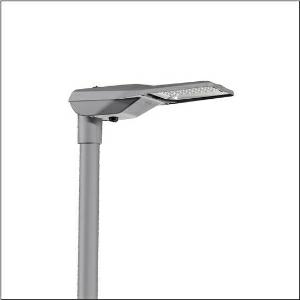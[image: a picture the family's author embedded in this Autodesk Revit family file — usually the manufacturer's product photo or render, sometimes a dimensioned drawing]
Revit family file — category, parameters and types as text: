
# Revit family: streetlight_sl_21_iq_mini___p0_8a_5xe2u31y08gb_4fe4
name_source: partatom
category: Lighting Fixtures
units: mm (PartAtom-declared; Revit-internal decimal feet)

## family parameters
Cut with Voids When Loaded = No
Host = Face
Light Source = No
Part Type = Normal
Room Calculation Point = No
Round Connector Dimension = Use Diameter
Shared = No

## types (1)
- --- (1 x LED, 6040 lm, 39.8 W, 3000K)
    Apparent Load = 40 VA
    CIE Flux Codes = 33 69 96 100 100
    Color Rendering = 70
    Color Temperature = 3000K
    Default Elevation = 1800 mm
    Description = Streetlight SL 21 iQ mini, mast luminaire, primary light control with lens, of PMMA, primary optical cover: cover, of toughened safety glass, transparent, light distribution: P0.8a, light emission: direct distribution, primary light characteristic: asymmetric, installation type: post-top, side-entry, LED, High Power LED, rated luminous flux: 6.040lm, luminous efficacy: 152lm/W, light colour: 730, colour temperature: 3000K, control gear: iQ-Street Remote, D4i with power reduction, control: pre-setting: logarithmic dimming characteristic, Street-Remote, Auto-Match, Temp-Guard, Lumen-Switch, Night-Set, Smart-Wire, Light-Fading, Desk-Remote (wireless, voltage-free reading and setting of iQ features in the workshop via application-optimized NFC function/RFID function), optimised constant luminous flux control (CLO 2.0), mains connection: 220..240V, AC, 50/60Hz, start of lifetime: 40W, end of service life: 41W, reduction: 18W, luminaire housing, of diecast aluminium, powder-coated, Siteco® metallic grey (DB 702S), corrosivity category C5 mid according to DIN EN ISO 12944, please order mast flange separately, inclination adjustable: 0°, 5°, 10°, 15°, sealing non-destructively replaceable, multi-level sealing system, length: 628mm, width: 235mm, height: 110mm, mast flange for spigot size: 42mm (side-entry): 5XC10008XM4, 60/48mm (side-entry/post-top): 5XC10108XM2, 76/60mm (side-entry/post-top): 5XC10108XM1, mounting height: 4..8m, Smart Interface below and above, protection rating (complete): IP66, insulation class (complete): insulation class II (safety insulation), certification: CE, ENEC, ENEC+, VDE, impact resistance: IK10, permissible operating ambient temperature for outdoor applications: -40..+50°C, standard-compliant lighting for roads and squares, packaging unit: 1 piece

Light Distribution: P0.8a
    Height = 110 mm
    Lamp = 1 x LED
    Lamp Light Flux = 6040 lm
    Lamp Power = 39.8 W
    Lamp count = 1
    Length = 625 mm
    Luminous efficacy = 152 lm/W
    Manufacturer = Siteco
    ModVariant = No
    Model = 5XE2U31Y08GB
    Number of Poles = 1
    OnlyDefault = Yes
    Power Factor = 1
    Product Name = Streetlight SL 21 iQ mini | P0.8a
    Product group = mast luminaire | pylon top
    ProductGroupID = 6100
    Protection Class = Protection class II
    Protection Degree = IP 66
    RLX_Detail_Level = 1
    RLX_Emergency_Light_Flux = 0 lm
    RLX_Emergency_Type = 0
    RLX_Emergency_Type_DB = No
    RlxData = <blob elided: 26553 chars, md5=028354a6>
    Socket = socket
    Standby Power = 0 W
    System Light Flux = 6040 lm
    System Power = 40 W
    Type Comments = factory setting: luminous flux: 100 % | dim-lin: 254 | 800 mA
    Type Image = l_1003514.jpg
    URL = http://relux.com
    VarID = @adj_074060
    Voltage = 0 V
    Weight = 0.00 kg
    Width = 234 mm

## geometry (parser evidence)
native form markers: Blend x4, Sweep x11
no freeform markers — native parametric forms only
